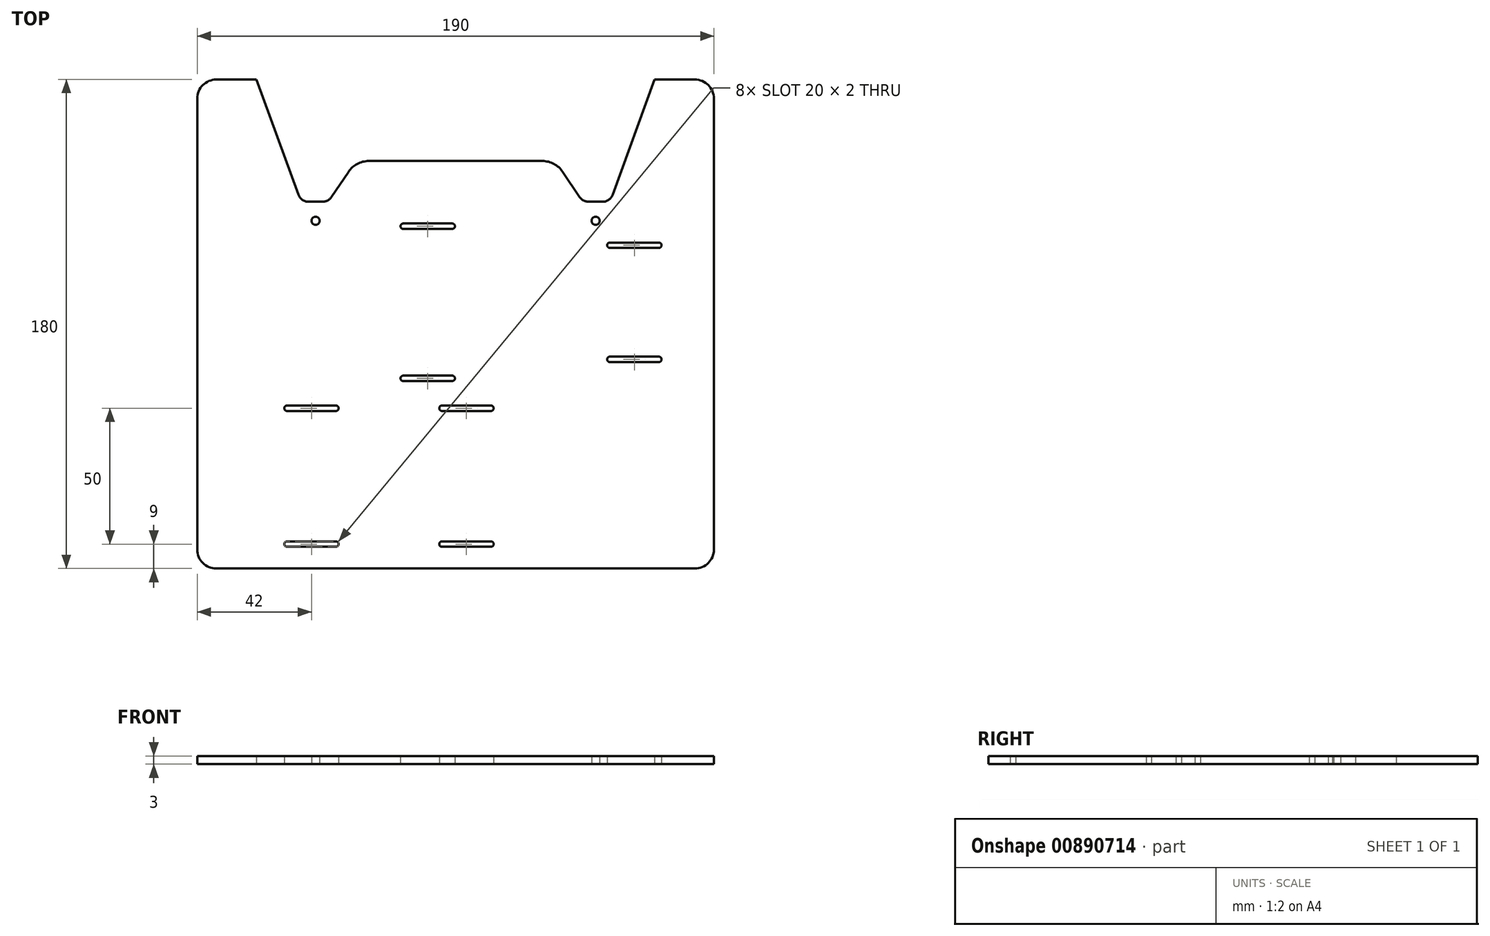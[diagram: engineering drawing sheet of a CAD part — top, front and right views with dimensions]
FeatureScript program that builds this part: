
annotation { "Feature Type Name" : "Feature", "Feature Type Description" : "" }
export const myFeature = defineFeature(function(context is Context, id is Id, definition is map)
    precondition{}
    {
        {
            var Q0;
            Q0=qCreatedBy(makeId("Top.planeOp"),FACE);
            var sketch = newSketch(context, id + "F0", { "sketchPlane" : qUnion([Q0])});
            skLineSegment(sketch, "E0", {"start": v(0, 7) * mm, "end": v(0, 173) * mm});
            skLineSegment(sketch, "E1", {"start": v(0, 239.85) * mm, "end": v(21.78, 180) * mm, "construction": true});
            skLineSegment(sketch, "E2", {"start": v(40.96, 135) * mm, "end": v(46.04, 135) * mm});
            skLineSegment(sketch, "E3", {"start": v(49.35, 136.76) * mm, "end": v(55.6, 146.03) * mm});
            skLineSegment(sketch, "E4", {"start": v(63.07, 150) * mm, "end": v(95, 150) * mm});
            skLineSegment(sketch, "E5", {"start": v(95, 0) * mm, "end": v(7, 0) * mm});
            skLineSegment(sketch, "E6", {"start": v(95, 150) * mm, "end": v(95, 0) * mm, "construction": true});
            skCircle(sketch, "E7", {"center": v(43.5, 128) * mm, "radius": 1.5 * mm});
            skLineSegment(sketch, "E8.MirrorCS", {"start": v(190, 7) * mm, "end": v(190, 173) * mm});
            skLineSegment(sketch, "E9.MirrorCS", {"start": v(190, 239.85) * mm, "end": v(168.22, 180) * mm, "construction": true});
            skLineSegment(sketch, "E10.MirrorCS", {"start": v(149.04, 135) * mm, "end": v(143.96, 135) * mm});
            skCircle(sketch, "E11.MirrorC", {"center": v(146.5, 128) * mm, "radius": 1.5 * mm});
            skLineSegment(sketch, "E12.MirrorCS", {"start": v(140.65, 136.76) * mm, "end": v(134.4, 146.03) * mm});
            skLineSegment(sketch, "E13.MirrorCS", {"start": v(126.93, 150) * mm, "end": v(95, 150) * mm});
            skLineSegment(sketch, "E14.MirrorCS", {"start": v(95, 0) * mm, "end": v(183, 0) * mm});
            skLineSegment(sketch, "E15", {"start": v(7, 180) * mm, "end": v(21.78, 180) * mm});
            skLineSegment(sketch, "E16.trimOffspring", {"start": v(168.22, 180) * mm, "end": v(183, 180) * mm});
            skLineSegment(sketch, "E17", {"start": v(0, 180) * mm, "end": v(0, 239.85) * mm, "construction": true});
            skLineSegment(sketch, "E18", {"start": v(21.78, 180) * mm, "end": v(21.78, 180) * mm});
            skLineSegment(sketch, "E19", {"start": v(21.78, 180) * mm, "end": v(37.2, 137.63) * mm});
            skLineSegment(sketch, "E20", {"start": v(190, 180) * mm, "end": v(190, 239.85) * mm, "construction": true});
            skLineSegment(sketch, "E21", {"start": v(168.22, 180) * mm, "end": v(152.8, 137.63) * mm});
            skPoint(sketch, "E22.visualSharp", {"position": v(58.28, 150) * mm});
            skArc(sketch, "E22.filletArc", {"start": v(63.07, 150) * mm, "mid": v(58.84, 148.95) * mm, "end": v(55.6, 146.03) * mm});
            skPoint(sketch, "E23.visualSharp", {"position": v(131.72, 150) * mm});
            skArc(sketch, "E23.filletArc", {"start": v(134.4, 146.03) * mm, "mid": v(131.16, 148.95) * mm, "end": v(126.93, 150) * mm});
            skPoint(sketch, "E24.visualSharp", {"position": v(38.16, 135) * mm});
            skArc(sketch, "E24.filletArc", {"start": v(37.2, 137.63) * mm, "mid": v(38.67, 135.72) * mm, "end": v(40.96, 135) * mm});
            skPoint(sketch, "E25.visualSharp", {"position": v(48.16, 135) * mm});
            skArc(sketch, "E25.filletArc", {"start": v(46.04, 135) * mm, "mid": v(47.91, 135.47) * mm, "end": v(49.35, 136.76) * mm});
            skPoint(sketch, "E26.visualSharp", {"position": v(141.84, 135) * mm});
            skArc(sketch, "E26.filletArc", {"start": v(140.65, 136.76) * mm, "mid": v(142.09, 135.47) * mm, "end": v(143.96, 135) * mm});
            skPoint(sketch, "E27.visualSharp", {"position": v(151.84, 135) * mm});
            skArc(sketch, "E27.filletArc", {"start": v(149.04, 135) * mm, "mid": v(151.33, 135.72) * mm, "end": v(152.8, 137.63) * mm});
            skPoint(sketch, "E28.visualSharp", {"position": v(0, 180) * mm});
            skArc(sketch, "E28.filletArc", {"start": v(7, 180) * mm, "mid": v(2.05, 177.95) * mm, "end": v(0, 173) * mm});
            skPoint(sketch, "E29.visualSharp", {"position": v(190, 180) * mm});
            skArc(sketch, "E29.filletArc", {"start": v(190, 173) * mm, "mid": v(187.95, 177.95) * mm, "end": v(183, 180) * mm});
            skPoint(sketch, "E30.visualSharp", {"position": v(190, 0) * mm});
            skArc(sketch, "E30.filletArc", {"start": v(183, 0) * mm, "mid": v(187.95, 2.05) * mm, "end": v(190, 7) * mm});
            skPoint(sketch, "E31.visualSharp", {"position": v(0, 0) * mm});
            skArc(sketch, "E31.filletArc", {"start": v(0, 7) * mm, "mid": v(2.05, 2.05) * mm, "end": v(7, 0) * mm});
            skLineSegment(sketch, "E32", {"start": v(74.75, 98) * mm, "end": v(170.75, 98) * mm, "construction": true});
            skLineSegment(sketch, "E33", {"start": v(151.75, 119) * mm, "end": v(169.75, 119) * mm});
            skLineSegment(sketch, "E34", {"start": v(75.75, 126) * mm, "end": v(93.75, 126) * mm});
            skLineSegment(sketch, "E35.MirrorCS", {"start": v(75.75, 70) * mm, "end": v(93.75, 70) * mm});
            skLineSegment(sketch, "E36", {"start": v(151.75, 77) * mm, "end": v(169.75, 77) * mm});
            skLineSegment(sketch, "E37", {"start": v(151.75, 119.3) * mm, "end": v(141.25, 119.3) * mm, "construction": true});
            skPoint(sketch, "E38", {"position": v(146.5, 119.3) * mm});
            skArc(sketch, "E39.0.startCap", {"start": v(75.75, 125) * mm, "mid": v(74.75, 126) * mm, "end": v(75.75, 127) * mm});
            skArc(sketch, "E39.0.endCap", {"start": v(93.75, 127) * mm, "mid": v(94.75, 126) * mm, "end": v(93.75, 125) * mm});
            skLineSegment(sketch, "E39.0.left", {"start": v(75.75, 127) * mm, "end": v(93.75, 127) * mm});
            skLineSegment(sketch, "E39.0.right", {"start": v(75.75, 125) * mm, "end": v(93.75, 125) * mm});
            skArc(sketch, "E39.1.startCap", {"start": v(151.75, 118) * mm, "mid": v(150.75, 119) * mm, "end": v(151.75, 120) * mm});
            skArc(sketch, "E39.1.endCap", {"start": v(169.75, 120) * mm, "mid": v(170.75, 119) * mm, "end": v(169.75, 118) * mm});
            skLineSegment(sketch, "E39.1.left", {"start": v(151.75, 120) * mm, "end": v(169.75, 120) * mm});
            skLineSegment(sketch, "E39.1.right", {"start": v(151.75, 118) * mm, "end": v(169.75, 118) * mm});
            skArc(sketch, "E39.2.startCap", {"start": v(151.75, 76) * mm, "mid": v(150.75, 77) * mm, "end": v(151.75, 78) * mm});
            skArc(sketch, "E39.2.endCap", {"start": v(169.75, 78) * mm, "mid": v(170.75, 77) * mm, "end": v(169.75, 76) * mm});
            skLineSegment(sketch, "E39.2.left", {"start": v(151.75, 78) * mm, "end": v(169.75, 78) * mm});
            skLineSegment(sketch, "E39.2.right", {"start": v(151.75, 76) * mm, "end": v(169.75, 76) * mm});
            skArc(sketch, "E39.3.startCap", {"start": v(75.75, 69) * mm, "mid": v(74.75, 70) * mm, "end": v(75.75, 71) * mm});
            skArc(sketch, "E39.3.endCap", {"start": v(93.75, 71) * mm, "mid": v(94.75, 70) * mm, "end": v(93.75, 69) * mm});
            skLineSegment(sketch, "E39.3.left", {"start": v(75.75, 71) * mm, "end": v(93.75, 71) * mm});
            skLineSegment(sketch, "E39.3.right", {"start": v(75.75, 69) * mm, "end": v(93.75, 69) * mm});
            skPoint(sketch, "E40", {"position": v(74.75, 126) * mm});
            skPoint(sketch, "E41", {"position": v(170.75, 119) * mm});
            skLineSegment(sketch, "E42", {"start": v(33, 34) * mm, "end": v(108, 34) * mm, "construction": true});
            skLineSegment(sketch, "E43", {"start": v(33, 59) * mm, "end": v(51, 59) * mm, "construction": true});
            skLineSegment(sketch, "E44", {"start": v(90, 59) * mm, "end": v(108, 59) * mm, "construction": true});
            skLineSegment(sketch, "E45.MirrorCS", {"start": v(33, 9) * mm, "end": v(51, 9) * mm, "construction": true});
            skLineSegment(sketch, "E46.MirrorCS", {"start": v(90, 9) * mm, "end": v(108, 9) * mm, "construction": true});
            skArc(sketch, "E47.0.startCap", {"start": v(33, 58) * mm, "mid": v(32, 59) * mm, "end": v(33, 60) * mm});
            skArc(sketch, "E47.0.endCap", {"start": v(51, 60) * mm, "mid": v(52, 59) * mm, "end": v(51, 58) * mm});
            skLineSegment(sketch, "E47.0.left", {"start": v(33, 60) * mm, "end": v(51, 60) * mm});
            skLineSegment(sketch, "E47.0.right", {"start": v(33, 58) * mm, "end": v(51, 58) * mm});
            skArc(sketch, "E47.1.startCap", {"start": v(90, 58) * mm, "mid": v(89, 59) * mm, "end": v(90, 60) * mm});
            skArc(sketch, "E47.1.endCap", {"start": v(108, 60) * mm, "mid": v(109, 59) * mm, "end": v(108, 58) * mm});
            skLineSegment(sketch, "E47.1.left", {"start": v(90, 60) * mm, "end": v(108, 60) * mm});
            skLineSegment(sketch, "E47.1.right", {"start": v(90, 58) * mm, "end": v(108, 58) * mm});
            skArc(sketch, "E47.2.startCap", {"start": v(33, 8) * mm, "mid": v(32, 9) * mm, "end": v(33, 10) * mm});
            skArc(sketch, "E47.2.endCap", {"start": v(51, 10) * mm, "mid": v(52, 9) * mm, "end": v(51, 8) * mm});
            skLineSegment(sketch, "E47.2.left", {"start": v(33, 10) * mm, "end": v(51, 10) * mm});
            skLineSegment(sketch, "E47.2.right", {"start": v(33, 8) * mm, "end": v(51, 8) * mm});
            skArc(sketch, "E47.3.startCap", {"start": v(90, 8) * mm, "mid": v(89, 9) * mm, "end": v(90, 10) * mm});
            skArc(sketch, "E47.3.endCap", {"start": v(108, 10) * mm, "mid": v(109, 9) * mm, "end": v(108, 8) * mm});
            skLineSegment(sketch, "E47.3.left", {"start": v(90, 10) * mm, "end": v(108, 10) * mm});
            skLineSegment(sketch, "E47.3.right", {"start": v(90, 8) * mm, "end": v(108, 8) * mm});
            skPoint(sketch, "E48", {"position": v(146.5, 135) * mm});
            skPoint(sketch, "E49", {"position": v(43.5, 135) * mm});
            skSolve(sketch);
        }
        {
            var Q0;
            Q0=makeQuery(id+"F0.imprint","IMPRINT",FACE,{"disambiguationData":[TD([[makeQuery(id+"F0.imprint","IMPRINT",EDGE,{"derivedFrom":sQuery(id+"F0.wireOp",EDGE,"E0")}),-1.0]])]});
            extrude(context, id + "F1", {"entities" : qUnion([Q0]), "depth" : 3 * mm, "offsetDistance" : 25 * mm});
        }
    });
